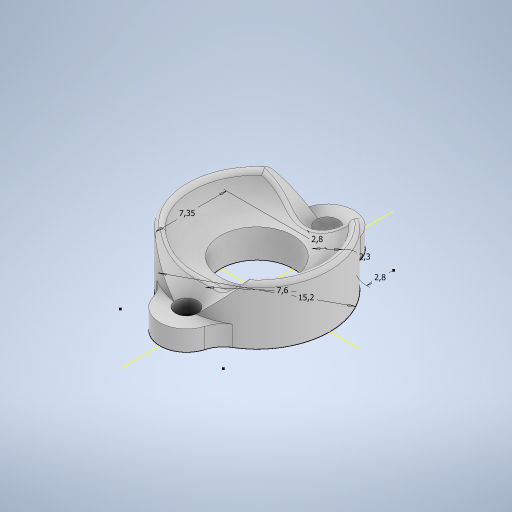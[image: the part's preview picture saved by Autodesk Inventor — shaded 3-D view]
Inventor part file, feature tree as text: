
AUTODESK INVENTOR PART (.ipt)
format: ipt  version: 2024.3 (Build 283343000, 343)  size: 376,320 bytes
history: native  units: in
note: dims shown in document units (in); Inventor stores cm internally (conversion verified against a paired STEP export)
features: extrude x2, fillet x2, sketch x1, chamfer x1
ambient origin geometry x8: Origin, YZ Plane, XZ Plane, XY Plane, X Axis, Y Axis, Z Axis, Center Point
bodies: Solid1 (feature_tree)
feature tree (6):
  sketch  "Sketch1"  dims[d0=0.2992in d1=0.5984in d2=0.0906in d3=0.2894in d4=0.1102in d5=0.1102in d6=0.0827in d7=0.0in d8=0.2362in d9=0.0in d10=0.1181in d11=0.1535in d12=0.0787in d13=45.0deg d14=0.0197in]
  extrude  "Extrusion1"  Depth=0.0197in
  extrude  "Extrusion2"  Depth=0.0197in
  fillet  "Fillet1"  Radius=0.2894in
  chamfer  "Chamfer1"  Distance=0.1102in
  fillet  "Fillet2"  Radius=0.1102in
